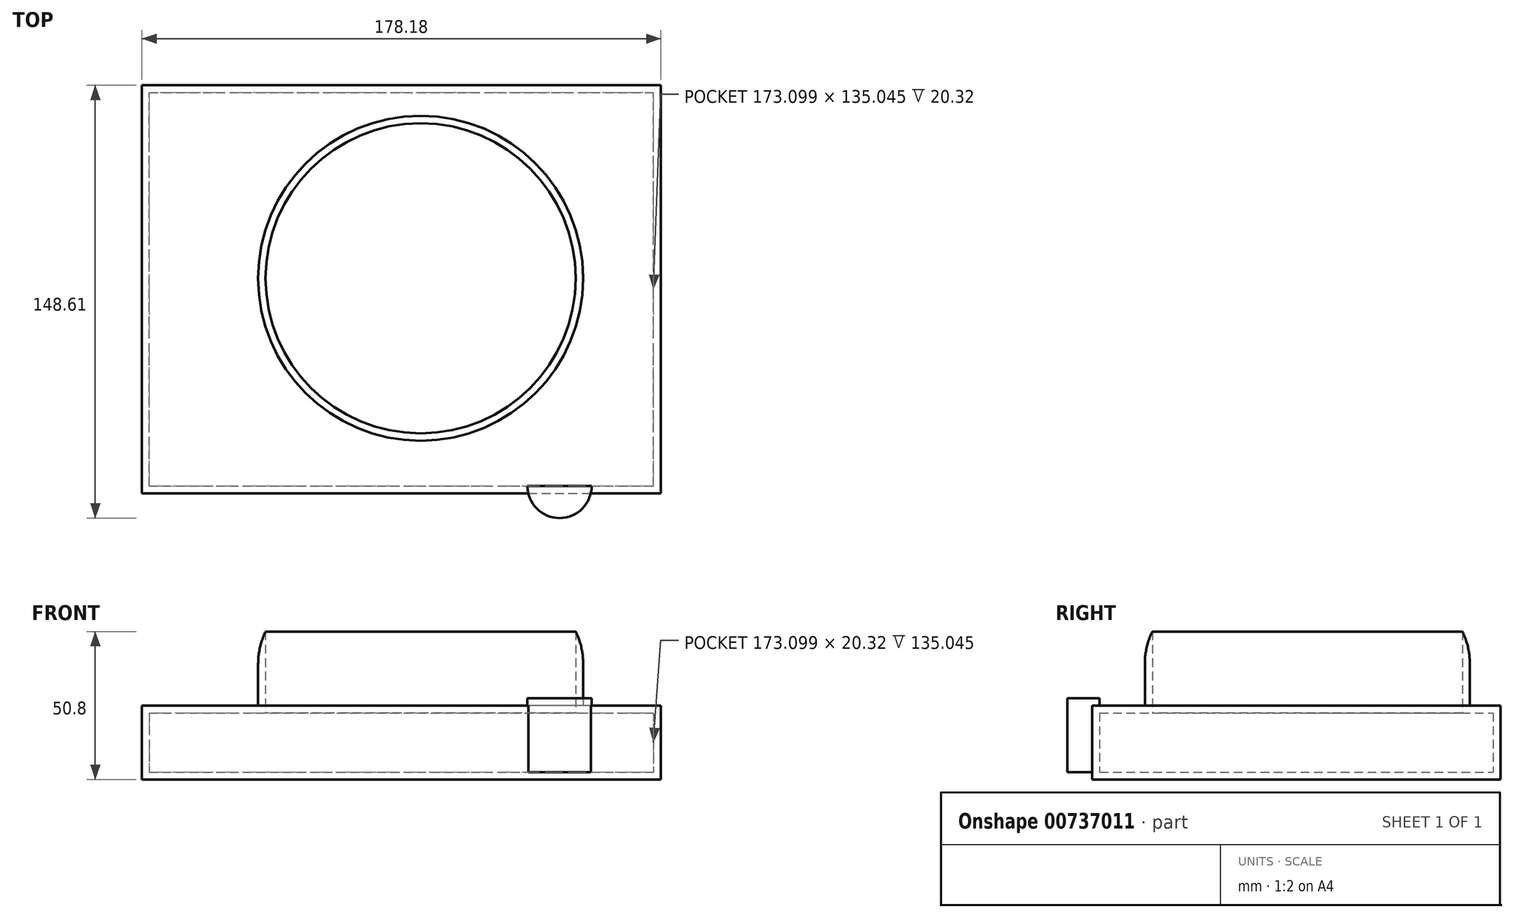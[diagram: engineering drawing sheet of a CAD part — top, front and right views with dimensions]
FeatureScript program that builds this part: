
annotation { "Feature Type Name" : "Feature", "Feature Type Description" : "" }
export const myFeature = defineFeature(function(context is Context, id is Id, definition is map)
    precondition{}
    {
        {
            var Q0;
            Q0=qCreatedBy(makeId("Top.planeOp"),FACE);
            var sketch = newSketch(context, id + "F0", { "sketchPlane" : qUnion([Q0])});
            skLineSegment(sketch, "E0.bottom", {"start": v(0, 0) * mm, "end": v(178.18, 0) * mm});
            skLineSegment(sketch, "E0.top", {"start": v(0, 140.12) * mm, "end": v(178.18, 140.12) * mm});
            skLineSegment(sketch, "E0.left", {"start": v(0, 0) * mm, "end": v(0, 140.12) * mm});
            skLineSegment(sketch, "E0.right", {"start": v(178.18, 0) * mm, "end": v(178.18, 140.12) * mm});
            skPoint(sketch, "E0.middle", {"position": v(89.09, 70.06) * mm});
            skSolve(sketch);
        }
        {
            var Q0;
            Q0 = qSketchRegion(id + "F0", true);
            extrude(context, id + "F1", {"entities" : qUnion([Q0]), "depth" : 25.4 * mm, "offsetDistance" : 25.4 * mm});
        }
        {
            var Q0;
            Q0=makeQuery(id+"F1.opExtrude","CAP_FACE",FACE,{"disambiguationData":[OSD([sQuery(id+"F0.wireOp",EDGE,"E0.bottom"),sQuery(id+"F0.wireOp",EDGE,"E0.top"),sQuery(id+"F0.wireOp",EDGE,"E0.left"),sQuery(id+"F0.wireOp",EDGE,"E0.right")])],"isStart":false});
            var sketch = newSketch(context, id + "F2", { "sketchPlane" : qUnion([Q0])});
            skCircle(sketch, "E1", {"center": v(95.7, 73.84) * mm, "radius": 55.79 * mm});
            skSolve(sketch);
        }
        {
            var Q0;
            Q0=makeQuery(id+"F2.imprint","IMPRINT",FACE,{"disambiguationData":[TD([[makeQuery(id+"F2.imprint","IMPRINT",EDGE,{"derivedFrom":sQuery(id+"F2.wireOp",EDGE,"E1")}),1.0]])]});
            extrude(context, id + "F3", {"entities" : qUnion([Q0]), "operationType" : NewBodyOperationType.ADD, "depth" : 25.4 * mm, "offsetDistance" : 25.4 * mm});
        }
        {
            var Q0;
            Q0=makeQuery(id+"F3.opExtrude","CAP_FACE",FACE,{"disambiguationData":[OSD([sQuery(id+"F2.wireOp",EDGE,"E1")])],"isStart":false});
            shell(context, id + "F4", {"entities" : qUnion([Q0]), "thickness" : 2.54 * mm});
        }
        {
            var Q0;
            Q0=makeQuery(id+"F3.opExtrude","CAP_EDGE",EDGE,{"disambiguationData":[OSD([sQuery(id+"F2.wireOp",EDGE,"E1")])],"isStart":false});
            fillet(context, id + "F5", {"entities" : qUnion([Q0]), "radius" : 25.4 * mm, "tangentPropagation" : true, "allowEdgeOverflow" : false});
        }
        {
            var Q0;
            {var subQ0=sQuery(id+"F0.wireOp",EDGE,"E0.right");var subQ1=sQuery(id+"F0.wireOp",EDGE,"E0.left");var subQ2=sQuery(id+"F0.wireOp",EDGE,"E0.top");var subQ3=sQuery(id+"F0.wireOp",EDGE,"E0.bottom");Q0=makeQuery(id+"F4.opShell","OFFSET_FACE",FACE,{"disambiguationData":[OSD([subQ3,subQ2,subQ1,subQ0]),TDD([makeQuery(id+"F1.opExtrude","CAP_FACE",FACE,{"disambiguationData":[OSD([subQ3,subQ2,subQ1,subQ0])],"isStart":true})])]});}
            var sketch = newSketch(context, id + "F6", { "sketchPlane" : qUnion([Q0])});
            skCircle(sketch, "E2", {"center": v(143.39, 2.54) * mm, "radius": 11.03 * mm});
            skSolve(sketch);
        }
        {
            var Q0;
            {var subQ0=sQuery(id+"F6.wireOp",EDGE,"E2");var subQ1=sQuery(id+"F0.wireOp",EDGE,"E0.bottom");var subQ2=makeQuery(id+"F4.opShell","OFFSET_EDGE",EDGE,{"disambiguationData":[OSD([subQ1]),TDD([makeQuery(id+"F1.opExtrude","CAP_EDGE",EDGE,{"disambiguationData":[OSD([subQ1])],"isStart":true})])]});var subQ3=makeQuery(id+"F6.imprint","INTERSECT",VERTEX,{"disambiguationData":[OD(0.0)],"derivedFrom":[subQ2,subQ0]});Q0=makeQuery(id+"F6.imprint","IMPRINT",FACE,{"disambiguationData":[TD([[makeQuery(id+"F6.imprint","IMPRINT",EDGE,{"disambiguationData":[TD([[subQ3,-1.0]])],"derivedFrom":subQ0}),1.0]])]});}
            extrude(context, id + "F7", {"entities" : qUnion([Q0]), "operationType" : NewBodyOperationType.ADD, "depth" : 25.4 * mm, "offsetDistance" : 25.4 * mm});
        }
    });
